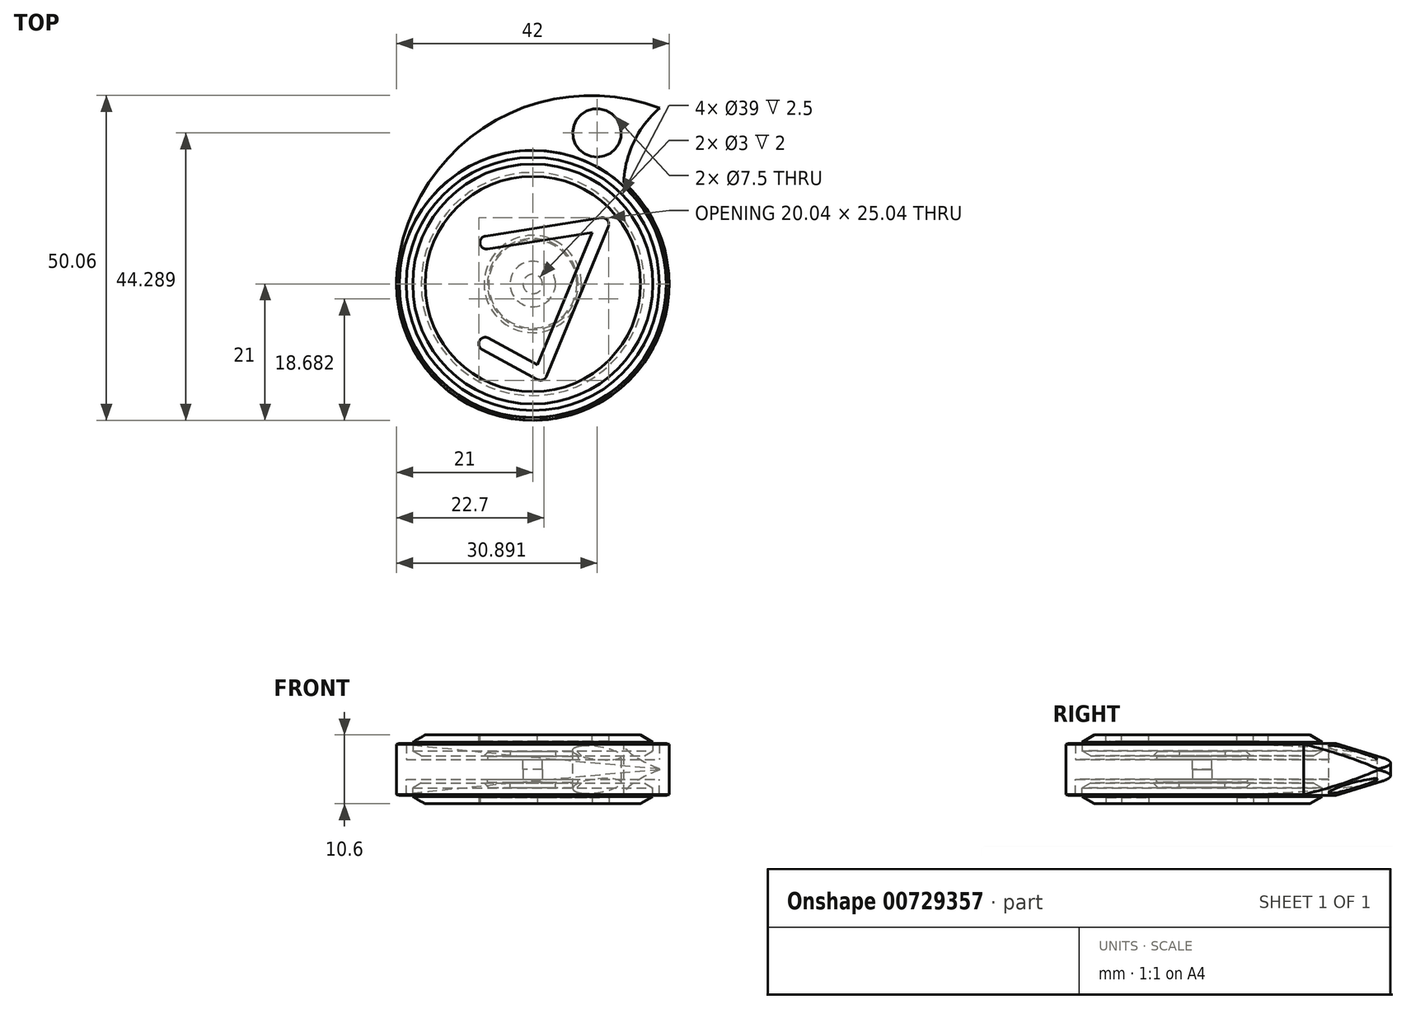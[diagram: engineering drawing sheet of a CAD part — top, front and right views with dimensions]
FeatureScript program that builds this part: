
annotation { "Feature Type Name" : "Feature", "Feature Type Description" : "" }
export const myFeature = defineFeature(function(context is Context, id is Id, definition is map)
    precondition{}
    {
        {
            var Q0;
            Q0=qCreatedBy(makeId("Top.planeOp"),FACE);
            var sketch = newSketch(context, id + "F0", { "sketchPlane" : qUnion([Q0])});
            skCircle(sketch, "E0", {"center": v(0, 0) * mm, "radius": 5 * mm});
            skCircle(sketch, "E1", {"center": v(0, 0) * mm, "radius": 1.5 * mm});
            skSolve(sketch);
        }
        {
            var Q0;
            Q0 = qSketchRegion(id + "F0", true);
            extrude(context, id + "F1", {"entities" : qUnion([Q0]), "depth" : 2 * mm, "offsetDistance" : 25 * mm});
        }
        {
            var Q0;
            Q0=qCreatedBy(makeId("Front.planeOp"),FACE);
            var sketch = newSketch(context, id + "F2", { "sketchPlane" : qUnion([Q0])});
            skLineSegment(sketch, "E2", {"start": v(-5, 0) * mm, "end": v(-5, 2) * mm});
            skLineSegment(sketch, "E3", {"start": v(-5, 0) * mm, "end": v(-21, 0) * mm});
            skLineSegment(sketch, "E4", {"start": v(-21, 0) * mm, "end": v(-21, 4) * mm});
            skLineSegment(sketch, "E5", {"start": v(-21, 4) * mm, "end": v(-19.5, 4) * mm});
            skLineSegment(sketch, "E6", {"start": v(-19.5, 4) * mm, "end": v(-19.5, 1.5) * mm});
            skLineSegment(sketch, "E7", {"start": v(-19.5, 1.5) * mm, "end": v(-7, 1.5) * mm});
            skLineSegment(sketch, "E8", {"start": v(-7, 1.5) * mm, "end": v(-7, 2) * mm});
            skLineSegment(sketch, "E9", {"start": v(-7, 2) * mm, "end": v(-5, 2) * mm});
            skLineSegment(sketch, "E10", {"start": v(0, 0) * mm, "end": v(0, 5.83) * mm, "construction": true});
            skLineSegment(sketch, "E11.0", {"start": v(-5, 2) * mm, "end": v(5, 2) * mm, "construction": true});
            skSolve(sketch);
        }
        {
            var Q0;
            Q0 = qSketchRegion(id + "F2", true);
            var Q1;
            Q1=sQuery(id+"F2.wireOp",EDGE,"E10");
            revolve(context, id + "F3", {"surfaceOperationType" : NewSurfaceOperationType.NEW, "entities" : qUnion([Q0]), "axis" : qUnion([Q1]), "revolveType" : RevolveType.FULL});
        }
        {
            var Q0;
            Q0=qCreatedBy(makeId("Front.planeOp"),FACE);
            var sketch = newSketch(context, id + "F4", { "sketchPlane" : qUnion([Q0])});
            skLineSegment(sketch, "E12", {"start": v(0, 5.3) * mm, "end": v(-16.6, 5.3) * mm});
            skLineSegment(sketch, "E13", {"start": v(-16.6, 5.3) * mm, "end": v(-18.5, 4.2) * mm});
            skLineSegment(sketch, "E14", {"start": v(-18.5, 4.2) * mm, "end": v(-18.5, 2.84) * mm});
            skLineSegment(sketch, "E15", {"start": v(-18.5, 2.84) * mm, "end": v(-17.2, 2.1) * mm});
            skLineSegment(sketch, "E16", {"start": v(-17.2, 2.1) * mm, "end": v(-7.5, 2.1) * mm});
            skLineSegment(sketch, "E17", {"start": v(-18.5, 3.52) * mm, "end": v(-15.02, 3.52) * mm, "construction": true});
            skLineSegment(sketch, "E18", {"start": v(19.5, 4) * mm, "end": v(19.5, 1.5) * mm});
            skLineSegment(sketch, "E19", {"start": v(-19.5, 1.5) * mm, "end": v(-19.5, 4) * mm});
            skLineSegment(sketch, "E20.0.0", {"start": v(-5, 2) * mm, "end": v(5, 2) * mm});
            skLineSegment(sketch, "E21", {"start": v(-7.5, 2.1) * mm, "end": v(-6.8, 2.8) * mm});
            skLineSegment(sketch, "E22", {"start": v(-7.5, 2.1) * mm, "end": v(-6.48, 2.1) * mm, "construction": true});
            skLineSegment(sketch, "E23", {"start": v(-6.8, 2.8) * mm, "end": v(-3.5, 2.8) * mm});
            skLineSegment(sketch, "E24", {"start": v(-3.5, 2.8) * mm, "end": v(-3.5, 2) * mm});
            skLineSegment(sketch, "E25", {"start": v(-1.5, 0) * mm, "end": v(0, 0) * mm});
            skLineSegment(sketch, "E26", {"start": v(0, 0) * mm, "end": v(0, 5.3) * mm});
            skLineSegment(sketch, "E27", {"start": v(-1.5, 0) * mm, "end": v(-1.5, 2) * mm});
            skLineSegment(sketch, "E28.0", {"start": v(21, 4) * mm, "end": v(-21, 4) * mm, "construction": true});
            skSolve(sketch);
        }
        {
            var Q0;
            Q0 = qSketchRegion(id + "F4", true);
            var Q1;
            Q1=sQuery(id+"F4.wireOp",EDGE,"E26");
            revolve(context, id + "F5", {"surfaceOperationType" : NewSurfaceOperationType.NEW, "entities" : qUnion([Q0]), "axis" : qUnion([Q1]), "revolveType" : RevolveType.FULL});
        }
        {
            var Q0;
            Q0=makeQuery(id+"F3.opRevolve","SWEPT_BODY",BODY,{"disambiguationData":[OSD([sQuery(id+"F2.wireOp",EDGE,"E2"),sQuery(id+"F2.wireOp",EDGE,"E3"),sQuery(id+"F2.wireOp",EDGE,"E4"),sQuery(id+"F2.wireOp",EDGE,"E5"),sQuery(id+"F2.wireOp",EDGE,"E6"),sQuery(id+"F2.wireOp",EDGE,"E7"),sQuery(id+"F2.wireOp",EDGE,"E8"),sQuery(id+"F2.wireOp",EDGE,"E9")])]});
            var Q1;
            Q1=qCreatedBy(makeId("Top.planeOp"),FACE);
            mirror(context, id + "F6", {"operationType" : NewBodyOperationType.ADD, "entities" : qUnion([Q0]), "mirrorPlane" : qUnion([Q1])});
        }
        {
            var Q0;
            Q0=qCreatedBy(makeId("Top.planeOp"),FACE);
            var sketch = newSketch(context, id + "F7", { "sketchPlane" : qUnion([Q0])});
            skCircle(sketch, "E29", {"center": v(9, -1) * mm, "radius": 30.06 * mm});
            skCircle(sketch, "E30.0", {"center": v(0, 0) * mm, "radius": 21 * mm});
            skCircle(sketch, "E31", {"center": v(30, 15) * mm, "radius": 16 * mm});
            skCircle(sketch, "E32", {"center": v(9.9, 23.29) * mm, "radius": 5.75 * mm, "construction": true});
            skCircle(sketch, "E33", {"center": v(9.9, 23.29) * mm, "radius": 3.75 * mm});
            skSolve(sketch);
        }
        {
            var Q0;
            Q0=makeQuery(id+"F7.imprint","IMPRINT",FACE,{"disambiguationData":[TD([[makeQuery(id+"F7.imprint","IMPRINT",EDGE,{"derivedFrom":sQuery(id+"F7.wireOp",EDGE,"E33")}),-1.0]])]});
            var Q1;
            Q1=makeQuery(id+"F3.opRevolve","SWEPT_FACE",FACE,{"disambiguationData":[OSD([sQuery(id+"F2.wireOp",EDGE,"E5")])]});
            var Q2;
            Q2=makeQuery(id+"F6.opPattern","COPY",FACE,{"derivedFrom":makeQuery(id+"F3.opRevolve","SWEPT_FACE",FACE,{"disambiguationData":[OSD([sQuery(id+"F2.wireOp",EDGE,"E5")])]}),"instanceName":"1"});
            extrude(context, id + "F8", {"entities" : qUnion([Q0]), "operationType" : NewBodyOperationType.ADD, "endBound" : BoundingType.UP_TO_SURFACE, "depth" : 25 * mm, "endBoundEntityFace" : qUnion([Q1]), "offsetDistance" : 25 * mm, "hasSecondDirection" : true, "secondDirectionBound" : SecondDirectionBoundingType.UP_TO_SURFACE, "secondDirectionOppositeDirection" : true, "secondDirectionDepth" : 25 * mm, "secondDirectionBoundEntityFace" : qUnion([Q2])});
        }
        {
            var Q0;
            Q0=qCreatedBy(makeId("Front.planeOp"),FACE);
            var sketch = newSketch(context, id + "F9", { "sketchPlane" : qUnion([Q0])});
            skPoint(sketch, "E34.0", {"position": v(-20.58, 4) * mm});
            skLineSegment(sketch, "E35.0", {"start": v(6.57, -4) * mm, "end": v(-33.29, -4) * mm, "construction": true});
            skLineSegment(sketch, "E36", {"start": v(-20.58, 4) * mm, "end": v(-20.58, -4) * mm});
            skLineSegment(sketch, "E37", {"start": v(-20.58, 4) * mm, "end": v(-34.62, 4) * mm});
            skLineSegment(sketch, "E38", {"start": v(-34.62, 4) * mm, "end": v(-34.62, -4) * mm});
            skLineSegment(sketch, "E39", {"start": v(-34.62, -4) * mm, "end": v(-20.58, -4) * mm});
            skLineSegment(sketch, "E40", {"start": v(-34.62, 0) * mm, "end": v(-23.4, 0) * mm, "construction": true});
            skLineSegment(sketch, "E41", {"start": v(-33.67, 0) * mm, "end": v(-20.58, 4) * mm});
            skLineSegment(sketch, "E42.MirrorCS", {"start": v(-33.67, 0) * mm, "end": v(-20.58, -4) * mm});
            skLineSegment(sketch, "E43", {"start": v(0, 0) * mm, "end": v(0, -2.7) * mm, "construction": true});
            skSolve(sketch);
        }
        {
            var Q0;
            {var subQ0=sQuery(id+"F9.wireOp",EDGE,"E37");Q0=makeQuery(id+"F9.imprint","IMPRINT",FACE,{"disambiguationData":[TD([[makeQuery(id+"F9.imprint","IMPRINT",EDGE,{"derivedFrom":subQ0}),1.0]])]});}
            var Q1;
            {var subQ0=sQuery(id+"F9.wireOp",EDGE,"E39");Q1=makeQuery(id+"F9.imprint","IMPRINT",FACE,{"disambiguationData":[TD([[makeQuery(id+"F9.imprint","IMPRINT",EDGE,{"derivedFrom":subQ0}),1.0]])]});}
            var Q2;
            Q2=sQuery(id+"F9.wireOp",EDGE,"E43");
            revolve(context, id + "F10", {"operationType" : NewBodyOperationType.REMOVE, "surfaceOperationType" : NewSurfaceOperationType.NEW, "entities" : qUnion([Q0, Q1]), "axis" : qUnion([Q2]), "revolveType" : RevolveType.FULL, "oppositeDirection" : true});
        }
        {
            var Q0;
            Q0=makeQuery(id+"F5.opRevolve","SWEPT_FACE",FACE,{"disambiguationData":[OSD([sQuery(id+"F4.wireOp",EDGE,"E12")])]});
            var sketch = newSketch(context, id + "F11", { "sketchPlane" : qUnion([Q0])});
            skLineSegment(sketch, "E44", {"start": v(-7.14, 6.4) * mm, "end": v(10.73, 9.2) * mm});
            skLineSegment(sketch, "E45", {"start": v(10.73, 9.2) * mm, "end": v(1.2, -13.84) * mm});
            skLineSegment(sketch, "E46", {"start": v(1.2, -13.84) * mm, "end": v(-7.33, -9.21) * mm});
            skArc(sketch, "E47.0.startCap", {"start": v(-6.99, 5.4) * mm, "mid": v(-8.13, 6.24) * mm, "end": v(-7.3, 7.38) * mm});
            skArc(sketch, "E47.0.endCap", {"start": v(10.57, 10.2) * mm, "mid": v(11.72, 9.36) * mm, "end": v(10.88, 8.22) * mm});
            skLineSegment(sketch, "E47.0.left", {"start": v(-7.3, 7.38) * mm, "end": v(10.57, 10.2) * mm});
            skLineSegment(sketch, "E47.0.right", {"start": v(-6.99, 5.4) * mm, "end": v(10.88, 8.22) * mm});
            skArc(sketch, "E47.1.startCap", {"start": v(9.8, 9.59) * mm, "mid": v(11.11, 10.13) * mm, "end": v(11.65, 8.82) * mm});
            skArc(sketch, "E47.1.endCap", {"start": v(2.13, -14.22) * mm, "mid": v(0.82, -14.76) * mm, "end": v(0.28, -13.46) * mm});
            skLineSegment(sketch, "E47.1.left", {"start": v(11.65, 8.82) * mm, "end": v(2.13, -14.22) * mm});
            skLineSegment(sketch, "E47.1.right", {"start": v(9.8, 9.59) * mm, "end": v(0.28, -13.46) * mm});
            skArc(sketch, "E47.2.startCap", {"start": v(1.68, -12.96) * mm, "mid": v(2.08, -14.32) * mm, "end": v(0.72, -14.72) * mm});
            skArc(sketch, "E47.2.endCap", {"start": v(-7.8, -10.1) * mm, "mid": v(-8.2, -8.73) * mm, "end": v(-6.85, -8.33) * mm});
            skLineSegment(sketch, "E47.2.left", {"start": v(0.72, -14.72) * mm, "end": v(-7.8, -10.1) * mm});
            skLineSegment(sketch, "E47.2.right", {"start": v(1.68, -12.96) * mm, "end": v(-6.85, -8.33) * mm});
            skSolve(sketch);
        }
        {
            var Q0;
            Q0 = qSketchRegion(id + "F11", true);
            extrude(context, id + "F12", {"entities" : qUnion([Q0]), "operationType" : NewBodyOperationType.REMOVE, "oppositeDirection" : true, "depth" : 1 * mm, "offsetDistance" : 25 * mm});
        }
        {
            var Q0;
            Q0=makeQuery(id+"F1.opExtrude","SWEPT_BODY",BODY,{"disambiguationData":[OSD([sQuery(id+"F0.wireOp",EDGE,"E0"),sQuery(id+"F0.wireOp",EDGE,"E1")])]});
            var Q1;
            Q1=qCreatedBy(makeId("Top.planeOp"),FACE);
            mirror(context, id + "F13", {"operationType" : NewBodyOperationType.ADD, "entities" : qUnion([Q0]), "mirrorPlane" : qUnion([Q1])});
        }
        {
            var Q0;
            Q0=makeQuery(id+"F5.opRevolve","SWEPT_BODY",BODY,{"disambiguationData":[OSD([sQuery(id+"F4.wireOp",EDGE,"E12"),sQuery(id+"F4.wireOp",EDGE,"E13"),sQuery(id+"F4.wireOp",EDGE,"E14"),sQuery(id+"F4.wireOp",EDGE,"E15"),sQuery(id+"F4.wireOp",EDGE,"E16"),sQuery(id+"F4.wireOp",EDGE,"E20.0.0"),sQuery(id+"F4.wireOp",EDGE,"E21"),sQuery(id+"F4.wireOp",EDGE,"E23"),sQuery(id+"F4.wireOp",EDGE,"E24"),sQuery(id+"F4.wireOp",EDGE,"E25"),sQuery(id+"F4.wireOp",EDGE,"E26"),sQuery(id+"F4.wireOp",EDGE,"E27")])]});
            var Q1;
            Q1=qCreatedBy(makeId("Top.planeOp"),FACE);
            mirror(context, id + "F14", {"entities" : qUnion([Q0]), "mirrorPlane" : qUnion([Q1])});
        }
    });
